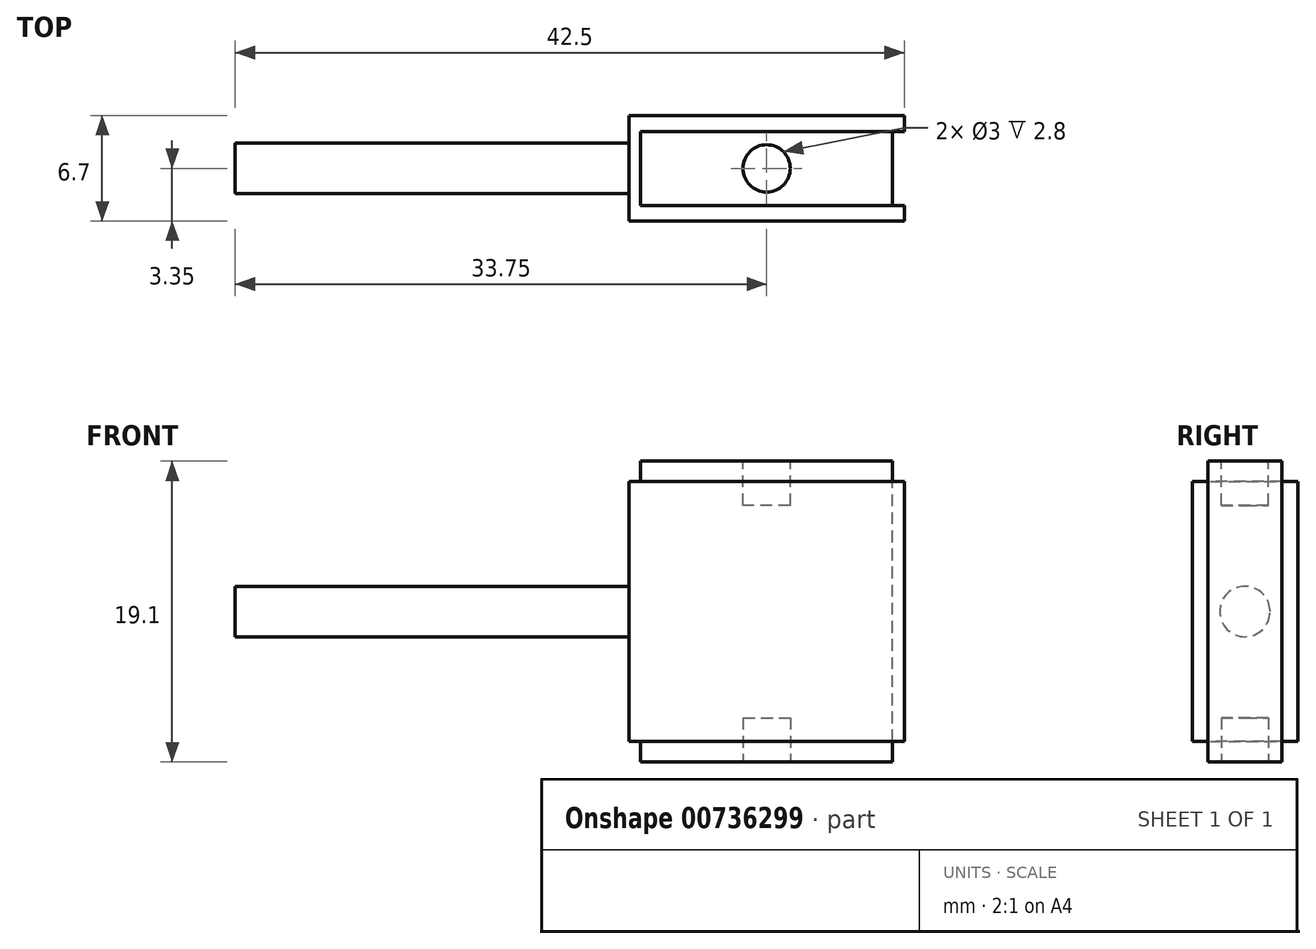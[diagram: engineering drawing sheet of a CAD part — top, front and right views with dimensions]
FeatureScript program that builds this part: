
annotation { "Feature Type Name" : "Feature", "Feature Type Description" : "" }
export const myFeature = defineFeature(function(context is Context, id is Id, definition is map)
    precondition{}
    {
        {
            var Q0;
            Q0=qCreatedBy(makeId("Front.planeOp"),FACE);
            var sketch = newSketch(context, id + "F0", { "sketchPlane" : qUnion([Q0])});
            skLineSegment(sketch, "E0.bottom", {"start": v(8, -9.55) * mm, "end": v(-8, -9.55) * mm});
            skLineSegment(sketch, "E0.top", {"start": v(8, 9.55) * mm, "end": v(-8, 9.55) * mm});
            skLineSegment(sketch, "E0.left", {"start": v(8, -9.55) * mm, "end": v(8, 9.55) * mm});
            skLineSegment(sketch, "E0.right", {"start": v(-8, -9.55) * mm, "end": v(-8, 9.55) * mm});
            skPoint(sketch, "E0.middle", {"position": v(0, 0) * mm});
            skSolve(sketch);
        }
        {
            var Q0;
            Q0 = qSketchRegion(id + "F0", true);
            extrude(context, id + "F1", {"entities" : qUnion([Q0]), "depth" : (4.7 / 2) * mm, "offsetDistance" : 25 * mm});
        }
        {
            var Q0;
            Q0=makeQuery(id+"F1.opExtrude","CAP_FACE",FACE,{"disambiguationData":[OSD([sQuery(id+"F0.wireOp",EDGE,"E0.bottom"),sQuery(id+"F0.wireOp",EDGE,"E0.top"),sQuery(id+"F0.wireOp",EDGE,"E0.left"),sQuery(id+"F0.wireOp",EDGE,"E0.right")])],"isStart":false});
            var sketch = newSketch(context, id + "F2", { "sketchPlane" : qUnion([Q0])});
            skLineSegment(sketch, "E1.bottom", {"start": v(8.75, -8.25) * mm, "end": v(-8.75, -8.25) * mm});
            skLineSegment(sketch, "E1.top", {"start": v(8.75, 8.25) * mm, "end": v(-8.75, 8.25) * mm});
            skLineSegment(sketch, "E1.left", {"start": v(8.75, -8.25) * mm, "end": v(8.75, 8.25) * mm});
            skLineSegment(sketch, "E1.right", {"start": v(-8.75, -8.25) * mm, "end": v(-8.75, 8.25) * mm});
            skPoint(sketch, "E1.middle", {"position": v(0, 0) * mm});
            skSolve(sketch);
        }
        {
            var Q0;
            Q0 = qSketchRegion(id + "F2", true);
            extrude(context, id + "F3", {"entities" : qUnion([Q0]), "operationType" : NewBodyOperationType.ADD, "depth" : (6.7 - 4.7) / 2 * mm, "offsetDistance" : 25 * mm});
        }
        {
            var Q0;
            {var subQ0=sQuery(id+"F2.wireOp",EDGE,"E1.top");var subQ1=sQuery(id+"F2.wireOp",EDGE,"E1.bottom");var subQ2=sQuery(id+"F0.wireOp",EDGE,"E0.right");var subQ3=sQuery(id+"F2.wireOp",EDGE,"E1.right");Q0=makeQuery(id+"F3.boolean.opBoolean","SPLIT",FACE,{"disambiguationData":[TD([makeQuery(id+"F1.opExtrude","SWEPT_FACE",FACE,{"disambiguationData":[OSD([subQ2])]})])],"derivedFrom":makeQuery(id+"F3.opExtrude","CAP_FACE",FACE,{"disambiguationData":[OSD([subQ1,subQ0,sQuery(id+"F2.wireOp",EDGE,"E1.left"),subQ3])],"isStart":true})});}
            var Q1;
            Q1=makeQuery(id+"F1.opExtrude","CAP_FACE",FACE,{"disambiguationData":[OSD([sQuery(id+"F0.wireOp",EDGE,"E0.bottom"),sQuery(id+"F0.wireOp",EDGE,"E0.top"),sQuery(id+"F0.wireOp",EDGE,"E0.left"),sQuery(id+"F0.wireOp",EDGE,"E0.right")])],"isStart":true});
            extrude(context, id + "F4", {"entities" : qUnion([Q0]), "operationType" : NewBodyOperationType.ADD, "endBound" : BoundingType.UP_TO_SURFACE, "depth" : 25 * mm, "endBoundEntityFace" : qUnion([Q1]), "offsetDistance" : 25 * mm});
        }
        {
            var Q0;
            Q0=makeQuery(id+"F1.opExtrude","SWEPT_BODY",BODY,{"disambiguationData":[OSD([sQuery(id+"F0.wireOp",EDGE,"E0.bottom"),sQuery(id+"F0.wireOp",EDGE,"E0.top"),sQuery(id+"F0.wireOp",EDGE,"E0.left"),sQuery(id+"F0.wireOp",EDGE,"E0.right")])]});
            var Q1;
            Q1=qCreatedBy(makeId("Front.planeOp"),FACE);
            mirror(context, id + "F5", {"operationType" : NewBodyOperationType.ADD, "entities" : qUnion([Q0]), "mirrorPlane" : qUnion([Q1])});
        }
        {
            var Q0;
            {var subQ0=sQuery(id+"F2.wireOp",EDGE,"E1.right");var subQ1=makeQuery(id+"F4.boolean.opBoolean","MERGE",FACE,{"derivedFrom":[makeQuery(id+"F3.opExtrude","SWEPT_FACE",FACE,{"disambiguationData":[OSD([subQ0])]}),makeQuery(id+"F4.opExtrude","SWEPT_FACE",FACE,{"disambiguationData":[OSD([subQ0])]})]});Q0=makeQuery(id+"F5.boolean.opBoolean","MERGE",FACE,{"derivedFrom":[subQ1,makeQuery(id+"F5.opPattern","COPY",FACE,{"derivedFrom":subQ1,"instanceName":"1"})]});}
            var sketch = newSketch(context, id + "F6", { "sketchPlane" : qUnion([Q0])});
            skCircle(sketch, "E2", {"center": v(0, 0) * mm, "radius": 1.6 * mm});
            skSolve(sketch);
        }
        {
            var Q0;
            Q0 = qSketchRegion(id + "F6", true);
            extrude(context, id + "F7", {"entities" : qUnion([Q0]), "operationType" : NewBodyOperationType.ADD, "depth" : 25 * mm, "offsetDistance" : 25 * mm});
        }
        {
            var Q0;
            {var subQ0=makeQuery(id+"F1.opExtrude","SWEPT_FACE",FACE,{"disambiguationData":[OSD([sQuery(id+"F0.wireOp",EDGE,"E0.top")])]});Q0=makeQuery(id+"F5.boolean.opBoolean","MERGE",FACE,{"derivedFrom":[subQ0,makeQuery(id+"F5.opPattern","COPY",FACE,{"derivedFrom":subQ0,"instanceName":"1"})]});}
            var sketch = newSketch(context, id + "F8", { "sketchPlane" : qUnion([Q0])});
            skCircle(sketch, "E3", {"center": v(0, 0) * mm, "radius": 1.5 * mm});
            skSolve(sketch);
        }
        {
            var Q0;
            Q0 = qSketchRegion(id + "F8", true);
            extrude(context, id + "F9", {"entities" : qUnion([Q0]), "operationType" : NewBodyOperationType.REMOVE, "oppositeDirection" : true, "depth" : 2.8 * mm, "offsetDistance" : 25 * mm});
        }
        {
            var Q0;
            {var subQ0=makeQuery(id+"F1.opExtrude","SWEPT_FACE",FACE,{"disambiguationData":[OSD([sQuery(id+"F0.wireOp",EDGE,"E0.bottom")])]});Q0=makeQuery(id+"F5.boolean.opBoolean","MERGE",FACE,{"derivedFrom":[subQ0,makeQuery(id+"F5.opPattern","COPY",FACE,{"derivedFrom":subQ0,"instanceName":"1"})]});}
            var sketch = newSketch(context, id + "F10", { "sketchPlane" : qUnion([Q0])});
            skCircle(sketch, "E4", {"center": v(0, 0) * mm, "radius": 1.5 * mm});
            skSolve(sketch);
        }
        {
            var Q0;
            Q0 = qSketchRegion(id + "F10", true);
            extrude(context, id + "F11", {"entities" : qUnion([Q0]), "operationType" : NewBodyOperationType.REMOVE, "oppositeDirection" : true, "depth" : 2.8 * mm, "offsetDistance" : 25 * mm});
        }
    });
